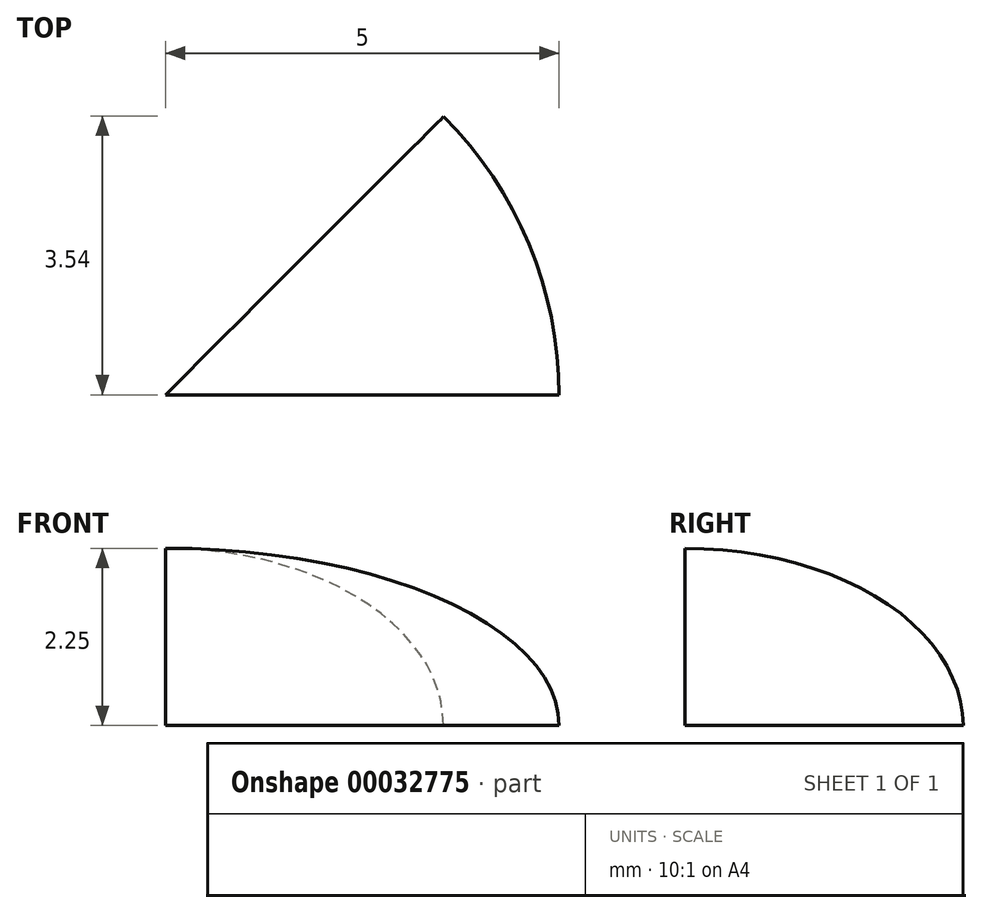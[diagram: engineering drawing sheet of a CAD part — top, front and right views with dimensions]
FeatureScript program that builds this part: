
annotation { "Feature Type Name" : "Feature", "Feature Type Description" : "" }
export const myFeature = defineFeature(function(context is Context, id is Id, definition is map)
    precondition{}
    {
        {
            var Q0;
            Q0=qCreatedBy(makeId("Front.planeOp"),FACE);
            var sketch = newSketch(context, id + "F0", { "sketchPlane" : qUnion([Q0])});
            skEllipticalArc(sketch, "E0", {});
            skLineSegment(sketch, "E1", {"start": v(0, 0) * mm, "end": v(0, 2.25) * mm});
            skPoint(sketch, "E1.endSnap0", {"position": v(0, 2.25) * mm});
            skLineSegment(sketch, "E2", {"start": v(0, 0) * mm, "end": v(5, 0) * mm});
            const initialGuessF0  = {"E0": [0, 0, 1, 0, 0.005, 0.00225, 0, 1.5707963267948966]};
            skSetInitialGuess(sketch, initialGuessF0);
            skSolve(sketch);
        }
        {
            var Q0;
            {var subQ0=sQuery(id+"F0.wireOp",EDGE,"E0");Q0=makeQuery(id+"F0.imprint","IMPRINT",FACE,{"disambiguationData":[TD([[makeQuery(id+"F0.imprint","IMPRINT",EDGE,{"derivedFrom":subQ0}),1.0]])]});}
            var Q1;
            Q1=sQuery(id+"F0.wireOp",EDGE,"E0");
            var Q2;
            Q2=sQuery(id+"F0.wireOp",EDGE,"E1");
            revolve(context, id + "F1", {"entities" : qUnion([Q0]), "surfaceEntities" : qUnion([Q1]), "axis" : qUnion([Q2]), "revolveType" : RevolveType.ONE_DIRECTION, "angle" : 45 * degree});
        }
    });
